# Revit family: CF-700
name_source: partatom
category: Обобщенные модели
revit_build: Autodesk Revit 2018 (Build: 20170223_1515(x64)
units: mm (PartAtom-declared; Revit-internal decimal feet)

## family parameters
Всегда вертикально = Да
Может служить основой для арматурных стержней = Нет
На основе рабочей плоскости = Нет
Общий = Нет
При загрузке вырезать с полостями = Нет
Размер круглого соединителя = Использовать диаметр
Тип детали = Нормальный
Точка расчета площади = Нет

## types (1)
- CF-700
    URL = https://www.horynize.ru
    Вес, кг = 32
    Габаритные размеры (ДхШхВ), мм = 667х353х339
    Изготовитель = Horynize
    Изображение типоразмера = <Нет>
    Кабель питания, мм = КГ 3х2,5 или ВВГнг 3х2,5 / КГ 5х2,5 или ВВГнг 5х2,5
    Код по классификатору = D3040100
    Количество скоростей = 10
    Комментарии к типоразмеру = Для подходит для помещений до 110м2
    Мощность вентилятора, кВт = 0,168
    Мощность воздухонагревателя, кВт = 4,4 (2,2х2)
    Напряжение питания, В/Гц = 220/50 и 380/50
    Описание = Приточная установка
    Производительность (max), м3/ч = 679
    Рабочая температура, С = -30...+50
    Стоимость = 154000 $
    Температура приточного воздуха = +7...+30
    Тип вентилятора = ЕС
    Уровень шума, дБ = 22-53
